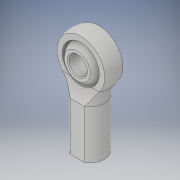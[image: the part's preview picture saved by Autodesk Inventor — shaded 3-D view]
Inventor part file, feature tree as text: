
AUTODESK INVENTOR PART (.ipt)
format: ipt  version: 2017 (Build 210142000, 142)  size: 662,528 bytes
history: native  units: in
note: dims shown in document units (in); Inventor stores cm internally (conversion verified against a paired STEP export)
features: other x1, chamfer x1
ambient origin geometry x8: Origin, YZ Plane, XZ Plane, XY Plane, X Axis, Y Axis, Z Axis, Center Point
bodies: Solid1 (feature_tree), Solid2 (feature_tree)
feature tree (2):
  other  "Cut-Extrude2"
  chamfer  "Chamfer1"  [1 undecoded]
note: 1 required parameter value undecoded (feature->parameter linkage not recoverable at this tier; creation-order binding heuristic only, values carry confidence <= 0.55)
